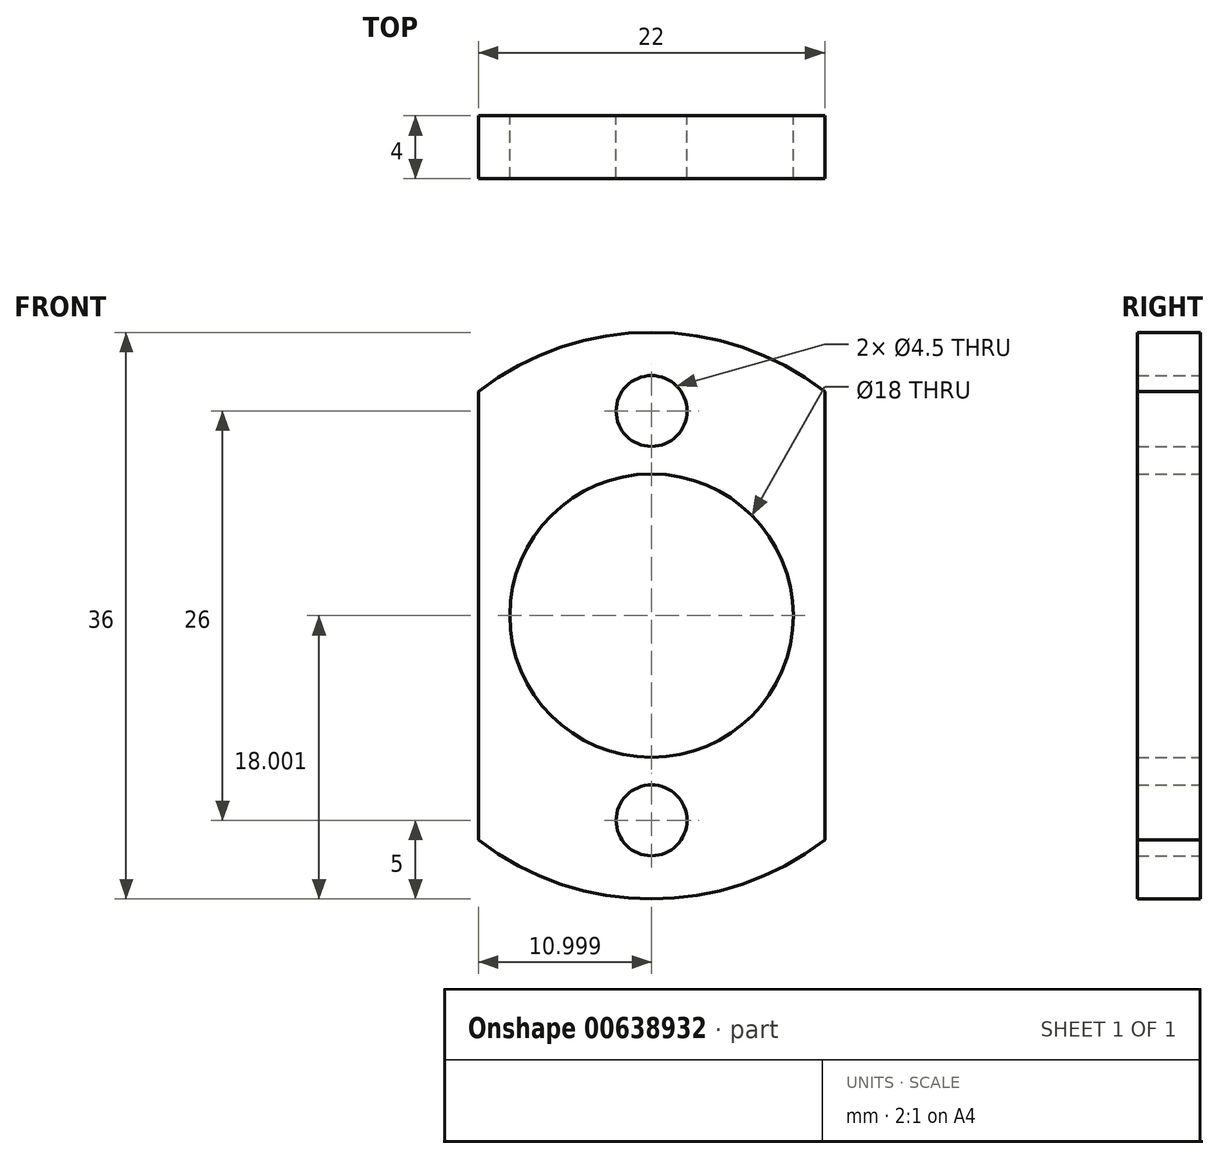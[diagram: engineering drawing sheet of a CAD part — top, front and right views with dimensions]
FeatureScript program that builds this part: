
annotation { "Feature Type Name" : "Feature", "Feature Type Description" : "" }
export const myFeature = defineFeature(function(context is Context, id is Id, definition is map)
    precondition{}
    {
        {
            var Q0;
            Q0=qCreatedBy(makeId("Front.planeOp"),FACE);
            var sketch = newSketch(context, id + "F0", { "sketchPlane" : qUnion([Q0])});
            skArc(sketch, "E0", {"start": v(15.26, 4.54) * mm, "mid": v(26.26, 0.8) * mm, "end": v(37.26, 4.54) * mm});
            skArc(sketch, "E1", {"start": v(37.26, 33.04) * mm, "mid": v(26.26, 36.8) * mm, "end": v(15.26, 33.04) * mm});
            skLineSegment(sketch, "E2", {"start": v(37.26, 4.54) * mm, "end": v(37.26, 33.04) * mm});
            skLineSegment(sketch, "E3", {"start": v(15.26, 33.04) * mm, "end": v(15.26, 4.54) * mm});
            skCircle(sketch, "E4", {"center": v(26.26, 18.8) * mm, "radius": 9 * mm});
            skCircle(sketch, "E5", {"center": v(26.26, 5.8) * mm, "radius": 2.25 * mm});
            skCircle(sketch, "E6", {"center": v(26.26, 31.8) * mm, "radius": 2.25 * mm});
            skLineSegment(sketch, "E7", {"start": v(26.26, 36.8) * mm, "end": v(26.26, 36.8) * mm});
            skLineSegment(sketch, "E8", {"start": v(26.26, 0.8) * mm, "end": v(26.26, 0.8) * mm});
            skArc(sketch, "E9", {"start": v(199.92, 123.8) * mm, "mid": v(201.26, 128.8) * mm, "end": v(199.92, 133.8) * mm});
            skLineSegment(sketch, "E10", {"start": v(192.26, 123.8) * mm, "end": v(196.76, 131.58) * mm});
            skLineSegment(sketch, "E11", {"start": v(192.26, 123.8) * mm, "end": v(190, 127.69) * mm});
            skLineSegment(sketch, "E12", {"start": v(190, 127.69) * mm, "end": v(194.5, 127.69) * mm});
            skArc(sketch, "E13", {"start": v(184.6, 133.8) * mm, "mid": v(183.26, 128.8) * mm, "end": v(184.6, 123.8) * mm});
            skLineSegment(sketch, "E14", {"start": v(176.26, 123.8) * mm, "end": v(180.76, 131.58) * mm});
            skLineSegment(sketch, "E15", {"start": v(176.26, 123.8) * mm, "end": v(174, 127.69) * mm});
            skLineSegment(sketch, "E16", {"start": v(174, 127.69) * mm, "end": v(178.5, 127.69) * mm});
            skSolve(sketch);
        }
        {
            var Q0;
            Q0 = qSketchRegion(id + "F0", true);
            extrude(context, id + "F1", {"entities" : qUnion([Q0]), "depth" : 4 * mm, "offsetDistance" : 25 * mm});
        }
        {
            var Q0;
            Q0=makeQuery(id+"F1.opExtrude","SWEPT_BODY",BODY,{"disambiguationData":[OSD([sQuery(id+"F0.wireOp",EDGE,"E14"),sQuery(id+"F0.wireOp",EDGE,"E15"),sQuery(id+"F0.wireOp",EDGE,"E16")])]});
            deleteBodies(context, id + "F2", {"entities" : qUnion([Q0])});
        }
        {
            var Q0;
            Q0=makeQuery(id+"F1.opExtrude","SWEPT_BODY",BODY,{"disambiguationData":[OSD([sQuery(id+"F0.wireOp",EDGE,"E10"),sQuery(id+"F0.wireOp",EDGE,"E11"),sQuery(id+"F0.wireOp",EDGE,"E12")])]});
            deleteBodies(context, id + "F3", {"entities" : qUnion([Q0])});
        }
    });
